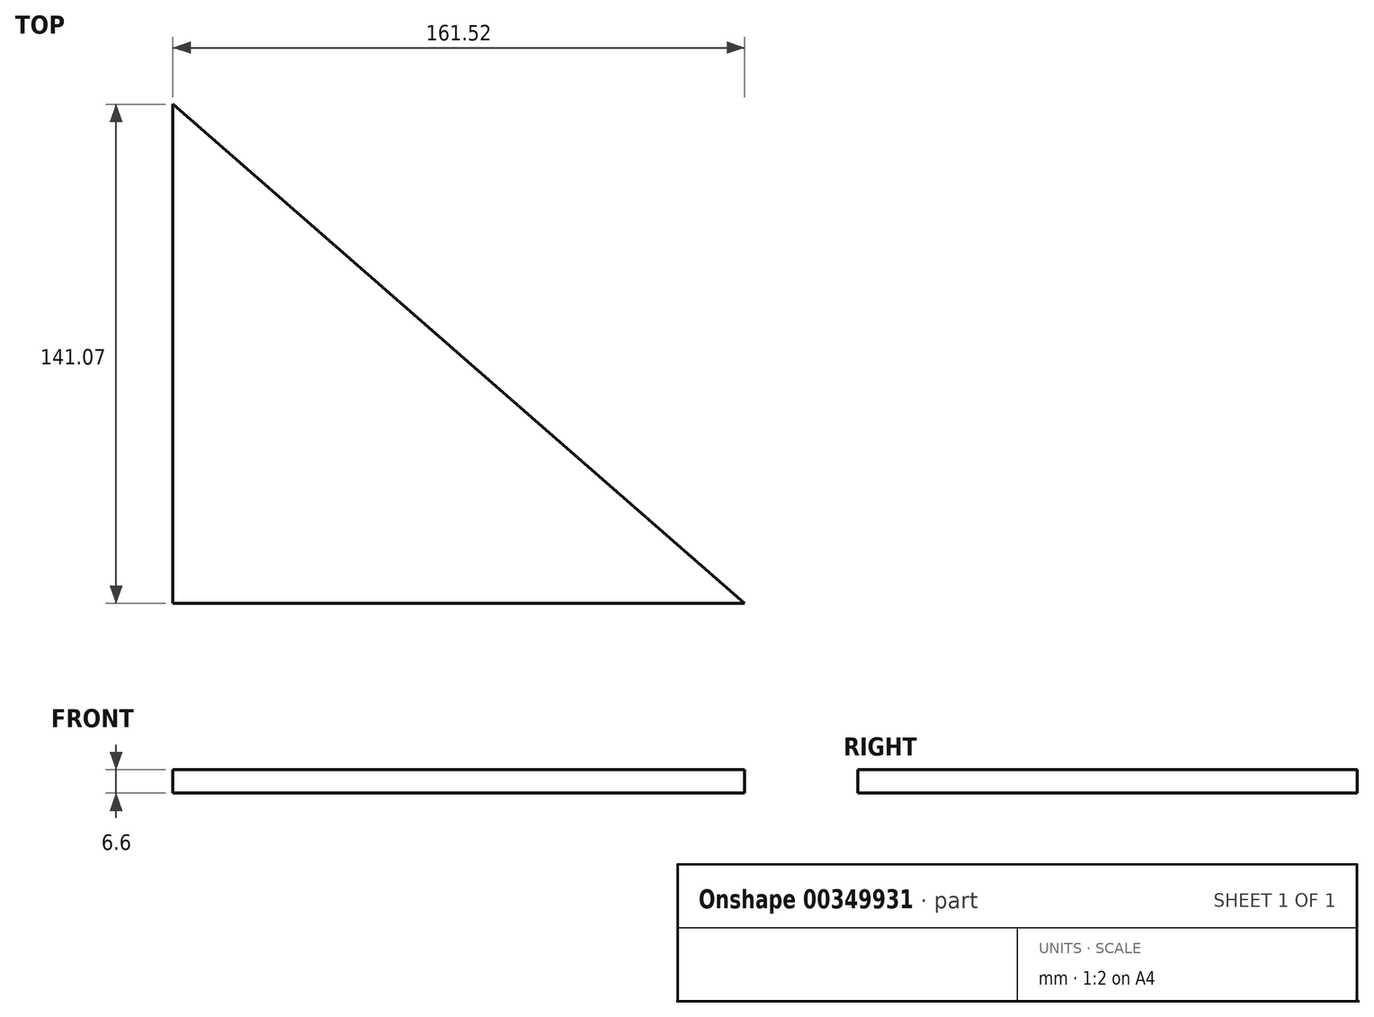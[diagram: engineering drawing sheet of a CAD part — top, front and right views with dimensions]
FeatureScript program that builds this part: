
annotation { "Feature Type Name" : "Feature", "Feature Type Description" : "" }
export const myFeature = defineFeature(function(context is Context, id is Id, definition is map)
    precondition{}
    {
        {
            var Q0;
            Q0=qCreatedBy(makeId("Top.planeOp"),FACE);
            var sketch = newSketch(context, id + "F0", { "sketchPlane" : qUnion([Q0])});
            skLineSegment(sketch, "E0", {"start": v(-69.33, 69.33) * mm, "end": v(-69.33, -71.74) * mm});
            skLineSegment(sketch, "E1", {"start": v(-69.33, -71.74) * mm, "end": v(92.2, -71.74) * mm});
            skLineSegment(sketch, "E2", {"start": v(92.2, -71.74) * mm, "end": v(-69.33, 69.33) * mm});
            skSolve(sketch);
        }
        {
            var Q0;
            Q0 = qSketchRegion(id + "F0", true);
            extrude(context, id + "F1", {"entities" : qUnion([Q0]), "depth" : 6.6 * mm, "offsetDistance" : 25.4 * mm});
        }
    });
